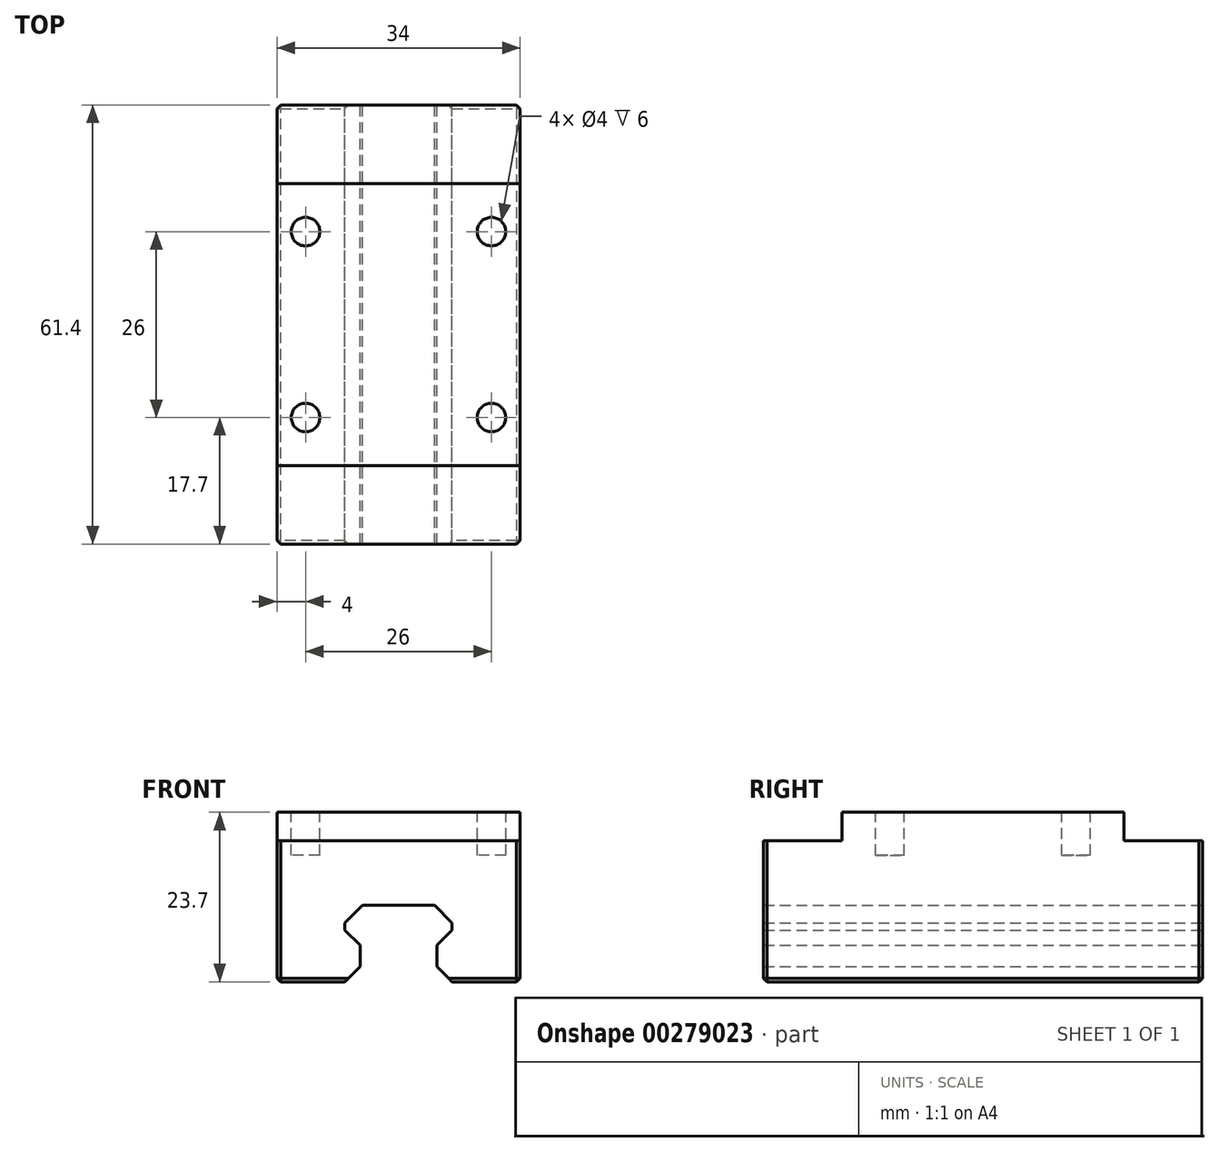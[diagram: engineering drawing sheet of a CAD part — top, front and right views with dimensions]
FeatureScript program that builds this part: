
annotation { "Feature Type Name" : "Feature", "Feature Type Description" : "" }
export const myFeature = defineFeature(function(context is Context, id is Id, definition is map)
    precondition{}
    {
        {
            var Q0;
            Q0=qCreatedBy(makeId("Front.planeOp"),FACE);
            var sketch = newSketch(context, id + "F0", { "sketchPlane" : qUnion([Q0])});
            skLineSegment(sketch, "E0", {"start": v(-7.5, -4.3) * mm, "end": v(-7.5, 0) * mm});
            skLineSegment(sketch, "E1", {"start": v(-7.5, 0) * mm, "end": v(-3.41, 0) * mm, "construction": true});
            skLineSegment(sketch, "E2", {"start": v(-7.5, 0) * mm, "end": v(-5.38, 2.12) * mm});
            skLineSegment(sketch, "E3", {"start": v(-5.38, 2.12) * mm, "end": v(-5.38, 5.12) * mm});
            skLineSegment(sketch, "E4", {"start": v(-9.32, 3.62) * mm, "end": v(-5.38, 3.62) * mm, "construction": true});
            skLineSegment(sketch, "E5", {"start": v(-5.38, 5.12) * mm, "end": v(-7.5, 7.24) * mm});
            skLineSegment(sketch, "E6", {"start": v(-7.5, 7.24) * mm, "end": v(-7.5, 8.24) * mm});
            skLineSegment(sketch, "E7", {"start": v(-7.5, 8.24) * mm, "end": v(-2.34, 8.24) * mm, "construction": true});
            skLineSegment(sketch, "E8", {"start": v(-7.5, 8.24) * mm, "end": v(-5.04, 10.7) * mm});
            skLineSegment(sketch, "E9", {"start": v(0, -6.24) * mm, "end": v(0, 12.64) * mm, "construction": true});
            skLineSegment(sketch, "E10", {"start": v(7.5, -4.3) * mm, "end": v(7.5, 0) * mm});
            skLineSegment(sketch, "E11", {"start": v(7.5, 0) * mm, "end": v(4.06, 0) * mm, "construction": true});
            skLineSegment(sketch, "E12", {"start": v(7.5, 0) * mm, "end": v(5.38, 2.12) * mm});
            skLineSegment(sketch, "E13", {"start": v(5.38, 2.12) * mm, "end": v(5.38, 5.12) * mm});
            skLineSegment(sketch, "E14", {"start": v(5.38, 5.12) * mm, "end": v(7.5, 7.24) * mm});
            skLineSegment(sketch, "E15", {"start": v(7.5, 7.24) * mm, "end": v(7.5, 8.24) * mm});
            skLineSegment(sketch, "E16", {"start": v(7.5, 8.24) * mm, "end": v(5.04, 10.7) * mm});
            skLineSegment(sketch, "E17", {"start": v(7.5, 8.24) * mm, "end": v(3.67, 8.24) * mm, "construction": true});
            skLineSegment(sketch, "E18", {"start": v(7.5, 7.24) * mm, "end": v(3.7, 7.24) * mm, "construction": true});
            skLineSegment(sketch, "E19", {"start": v(-7.5, 7.24) * mm, "end": v(-3.2, 7.24) * mm, "construction": true});
            skLineSegment(sketch, "E20", {"start": v(-5.04, 10.7) * mm, "end": v(5.04, 10.7) * mm});
            skLineSegment(sketch, "E21", {"start": v(-7.5, -4.3) * mm, "end": v(7.5, -4.3) * mm});
            skLineSegment(sketch, "E22", {"start": v(-7.5, 0) * mm, "end": v(7.5, 0) * mm});
            skPoint(sketch, "E23", {"position": v(0, 0) * mm});
            skLineSegment(sketch, "E24", {"start": v(-7.5, 0) * mm, "end": v(-17, 0) * mm});
            skLineSegment(sketch, "E25", {"start": v(-7.5, -4.3) * mm, "end": v(-17, -4.3) * mm, "construction": true});
            skLineSegment(sketch, "E26", {"start": v(-17, 0) * mm, "end": v(-17, 23.7) * mm});
            skLineSegment(sketch, "E27.MirrorCS", {"start": v(7.5, 0) * mm, "end": v(17, 0) * mm});
            skLineSegment(sketch, "E28.MirrorCS", {"start": v(17, 0) * mm, "end": v(17, 23.7) * mm});
            skLineSegment(sketch, "E29", {"start": v(-17, 23.7) * mm, "end": v(17, 23.7) * mm});
            skSolve(sketch);
        }
        {
            var Q0;
            Q0=makeQuery(id+"F0.imprint","IMPRINT",FACE,{"disambiguationData":[TD([[makeQuery(id+"F0.imprint","IMPRINT",EDGE,{"derivedFrom":sQuery(id+"F0.wireOp",EDGE,"E2")}),1.0]])]});
            extrude(context, id + "F1", {"entities" : qUnion([Q0]), "endBound" : BoundingType.SYMMETRIC, "depth" : 61.4 * mm});
        }
        {
            var Q0;
            Q0=makeQuery(id+"F1.opExtrude","SWEPT_FACE",FACE,{"disambiguationData":[OSD([sQuery(id+"F0.wireOp",EDGE,"E29")])]});
            var sketch = newSketch(context, id + "F2", { "sketchPlane" : qUnion([Q0])});
            skLineSegment(sketch, "E30.0", {"start": v(13, -30.7) * mm, "end": v(13, 30.7) * mm, "construction": true});
            skLineSegment(sketch, "E31.0", {"start": v(-13, -30.7) * mm, "end": v(-13, 30.7) * mm, "construction": true});
            skLineSegment(sketch, "E32", {"start": v(-13, 0) * mm, "end": v(13, 0) * mm, "construction": true});
            skLineSegment(sketch, "E33.0", {"start": v(-13, 13) * mm, "end": v(13, 13) * mm, "construction": true});
            skLineSegment(sketch, "E34.0", {"start": v(-13, -13) * mm, "end": v(13, -13) * mm, "construction": true});
            skCircle(sketch, "E35", {"center": v(-13, 13) * mm, "radius": 2 * mm});
            skCircle(sketch, "E36", {"center": v(13, 13) * mm, "radius": 2 * mm});
            skCircle(sketch, "E37", {"center": v(-13, -13) * mm, "radius": 2 * mm});
            skCircle(sketch, "E38", {"center": v(13, -13) * mm, "radius": 2 * mm});
            skLineSegment(sketch, "E39.0", {"start": v(-17, -19.7) * mm, "end": v(17, -19.7) * mm});
            skLineSegment(sketch, "E40.0", {"start": v(-17, 19.7) * mm, "end": v(17, 19.7) * mm});
            skSolve(sketch);
        }
        {
            var Q0;
            Q0=makeQuery(id+"F2.imprint","IMPRINT",FACE,{"disambiguationData":[TD([[makeQuery(id+"F2.imprint","IMPRINT",EDGE,{"derivedFrom":sQuery(id+"F2.wireOp",EDGE,"E35")}),1.0]])]});
            var Q1;
            Q1=makeQuery(id+"F2.imprint","IMPRINT",FACE,{"disambiguationData":[TD([[makeQuery(id+"F2.imprint","IMPRINT",EDGE,{"derivedFrom":sQuery(id+"F2.wireOp",EDGE,"E36")}),1.0]])]});
            var Q2;
            Q2=makeQuery(id+"F2.imprint","IMPRINT",FACE,{"disambiguationData":[TD([[makeQuery(id+"F2.imprint","IMPRINT",EDGE,{"derivedFrom":sQuery(id+"F2.wireOp",EDGE,"E38")}),1.0]])]});
            var Q3;
            Q3=makeQuery(id+"F2.imprint","IMPRINT",FACE,{"disambiguationData":[TD([[makeQuery(id+"F2.imprint","IMPRINT",EDGE,{"derivedFrom":sQuery(id+"F2.wireOp",EDGE,"E37")}),1.0]])]});
            extrude(context, id + "F3", {"entities" : qUnion([Q0, Q1, Q2, Q3]), "operationType" : NewBodyOperationType.REMOVE, "oppositeDirection" : true, "depth" : 6 * mm});
        }
        {
            var Q0;
            {var subQ0=sQuery(id+"F2.wireOp",EDGE,"E40.0");Q0=makeQuery(id+"F2.imprint","IMPRINT",FACE,{"disambiguationData":[TD([[makeQuery(id+"F2.imprint","IMPRINT",EDGE,{"derivedFrom":subQ0}),1.0]])]});}
            var Q1;
            {var subQ0=sQuery(id+"F2.wireOp",EDGE,"E39.0");Q1=makeQuery(id+"F2.imprint","IMPRINT",FACE,{"disambiguationData":[TD([[makeQuery(id+"F2.imprint","IMPRINT",EDGE,{"derivedFrom":subQ0}),-1.0]])]});}
            extrude(context, id + "F4", {"entities" : qUnion([Q0, Q1]), "operationType" : NewBodyOperationType.REMOVE, "oppositeDirection" : true, "depth" : 4 * mm});
        }
        {
            var Q0;
            Q0=makeQuery(id+"F1.opExtrude","SWEPT_EDGE",EDGE,{"disambiguationData":[OSD([sQuery(id+"F0.wireOp",EDGE,"E27.MirrorCS"),sQuery(id+"F0.wireOp",EDGE,"E28.MirrorCS")])]});
            var Q1;
            Q1=makeQuery(id+"F1.opExtrude","SWEPT_EDGE",EDGE,{"disambiguationData":[OSD([sQuery(id+"F0.wireOp",EDGE,"E24"),sQuery(id+"F0.wireOp",EDGE,"E26")])]});
            var Q2;
            {var subQ0=sQuery(id+"F0.wireOp",EDGE,"E29");Q2=makeQuery(id+"F4.boolean.opBoolean","COPY",EDGE,{"derivedFrom":makeQuery(id+"F4.opExtrude","CAP_EDGE",EDGE,{"disambiguationData":[OSD([subQ0]),TDD([makeQuery(id+"F2.imprint","IMPRINT",EDGE,{"derivedFrom":makeQuery(id+"F1.opExtrude","CAP_EDGE",EDGE,{"disambiguationData":[OSD([subQ0])],"isStart":false})})])],"isStart":false})});}
            var Q3;
            {var subQ0=sQuery(id+"F0.wireOp",EDGE,"E29");var subQ1=sQuery(id+"F0.wireOp",EDGE,"E26");var subQ2=makeQuery(id+"F1.opExtrude","SWEPT_EDGE",EDGE,{"disambiguationData":[OSD([subQ1,subQ0])]});Q3=makeQuery(id+"F4.boolean.opBoolean","COPY",EDGE,{"derivedFrom":makeQuery(id+"F4.opExtrude","CAP_EDGE",EDGE,{"disambiguationData":[OSD([subQ1,subQ0]),TDD([makeQuery(id+"F2.imprint","IMPRINT",EDGE,{"disambiguationData":[TD([[makeQuery(id+"F2.imprint","INTERSECT",VERTEX,{"derivedFrom":[subQ2,makeQuery(id+"F1.opExtrude","CAP_EDGE",EDGE,{"disambiguationData":[OSD([subQ0])],"isStart":false})]}),-1.0]])],"derivedFrom":subQ2})])],"isStart":false})});}
            var Q4;
            Q4=makeQuery(id+"F1.opExtrude","CAP_EDGE",EDGE,{"disambiguationData":[OSD([sQuery(id+"F0.wireOp",EDGE,"E28.MirrorCS")])],"isStart":false});
            var Q5;
            Q5=makeQuery(id+"F1.opExtrude","CAP_EDGE",EDGE,{"disambiguationData":[OSD([sQuery(id+"F0.wireOp",EDGE,"E26")])],"isStart":false});
            var Q6;
            {var subQ0=sQuery(id+"F0.wireOp",EDGE,"E29");Q6=makeQuery(id+"F4.boolean.opBoolean","COPY",EDGE,{"derivedFrom":makeQuery(id+"F4.opExtrude","CAP_EDGE",EDGE,{"disambiguationData":[OSD([subQ0]),TDD([makeQuery(id+"F2.imprint","IMPRINT",EDGE,{"derivedFrom":makeQuery(id+"F1.opExtrude","CAP_EDGE",EDGE,{"disambiguationData":[OSD([subQ0])],"isStart":true})})])],"isStart":false})});}
            var Q7;
            Q7=makeQuery(id+"F1.opExtrude","CAP_EDGE",EDGE,{"disambiguationData":[OSD([sQuery(id+"F0.wireOp",EDGE,"E28.MirrorCS")])],"isStart":true});
            var Q8;
            Q8=makeQuery(id+"F1.opExtrude","CAP_EDGE",EDGE,{"disambiguationData":[OSD([sQuery(id+"F0.wireOp",EDGE,"E26")])],"isStart":true});
            var Q9;
            Q9=makeQuery(id+"F1.opExtrude","CAP_EDGE",EDGE,{"disambiguationData":[OSD([sQuery(id+"F0.wireOp",EDGE,"E27.MirrorCS")])],"isStart":true});
            var Q10;
            Q10=makeQuery(id+"F1.opExtrude","CAP_EDGE",EDGE,{"disambiguationData":[OSD([sQuery(id+"F0.wireOp",EDGE,"E24")])],"isStart":true});
            var Q11;
            Q11=makeQuery(id+"F1.opExtrude","CAP_EDGE",EDGE,{"disambiguationData":[OSD([sQuery(id+"F0.wireOp",EDGE,"E24")])],"isStart":false});
            var Q12;
            Q12=makeQuery(id+"F1.opExtrude","CAP_EDGE",EDGE,{"disambiguationData":[OSD([sQuery(id+"F0.wireOp",EDGE,"E27.MirrorCS")])],"isStart":false});
            var Q13;
            {var subQ0=sQuery(id+"F0.wireOp",EDGE,"E29");var subQ1=sQuery(id+"F0.wireOp",EDGE,"E28.MirrorCS");var subQ2=makeQuery(id+"F1.opExtrude","SWEPT_EDGE",EDGE,{"disambiguationData":[OSD([subQ1,subQ0])]});Q13=makeQuery(id+"F4.boolean.opBoolean","COPY",EDGE,{"derivedFrom":makeQuery(id+"F4.opExtrude","CAP_EDGE",EDGE,{"disambiguationData":[OSD([subQ1,subQ0]),TDD([makeQuery(id+"F2.imprint","IMPRINT",EDGE,{"disambiguationData":[TD([[makeQuery(id+"F2.imprint","INTERSECT",VERTEX,{"derivedFrom":[subQ2,makeQuery(id+"F1.opExtrude","CAP_EDGE",EDGE,{"disambiguationData":[OSD([subQ0])],"isStart":false})]}),-1.0]])],"derivedFrom":subQ2})])],"isStart":false})});}
            var Q14;
            {var subQ0=sQuery(id+"F0.wireOp",EDGE,"E29");var subQ1=sQuery(id+"F0.wireOp",EDGE,"E26");var subQ2=makeQuery(id+"F1.opExtrude","SWEPT_EDGE",EDGE,{"disambiguationData":[OSD([subQ1,subQ0])]});Q14=makeQuery(id+"F4.boolean.opBoolean","COPY",EDGE,{"derivedFrom":makeQuery(id+"F4.opExtrude","CAP_EDGE",EDGE,{"disambiguationData":[OSD([subQ1,subQ0]),TDD([makeQuery(id+"F2.imprint","IMPRINT",EDGE,{"disambiguationData":[TD([[makeQuery(id+"F2.imprint","INTERSECT",VERTEX,{"derivedFrom":[subQ2,makeQuery(id+"F1.opExtrude","CAP_EDGE",EDGE,{"disambiguationData":[OSD([subQ0])],"isStart":true})]}),1.0]])],"derivedFrom":subQ2})])],"isStart":false})});}
            var Q15;
            {var subQ0=sQuery(id+"F0.wireOp",EDGE,"E29");var subQ1=sQuery(id+"F0.wireOp",EDGE,"E28.MirrorCS");var subQ2=makeQuery(id+"F1.opExtrude","SWEPT_EDGE",EDGE,{"disambiguationData":[OSD([subQ1,subQ0])]});Q15=makeQuery(id+"F4.boolean.opBoolean","COPY",EDGE,{"derivedFrom":makeQuery(id+"F4.opExtrude","CAP_EDGE",EDGE,{"disambiguationData":[OSD([subQ1,subQ0]),TDD([makeQuery(id+"F2.imprint","IMPRINT",EDGE,{"disambiguationData":[TD([[makeQuery(id+"F2.imprint","INTERSECT",VERTEX,{"derivedFrom":[subQ2,makeQuery(id+"F1.opExtrude","CAP_EDGE",EDGE,{"disambiguationData":[OSD([subQ0])],"isStart":true})]}),1.0]])],"derivedFrom":subQ2})])],"isStart":false})});}
            chamfer(context, id + "F5", {"entities" : qUnion([Q0, Q1, Q2, Q3, Q4, Q5, Q6, Q7, Q8, Q9, Q10, Q11, Q12, Q13, Q14, Q15]), "width" : .5 * mm, "tangentPropagation" : true});
        }
    });
